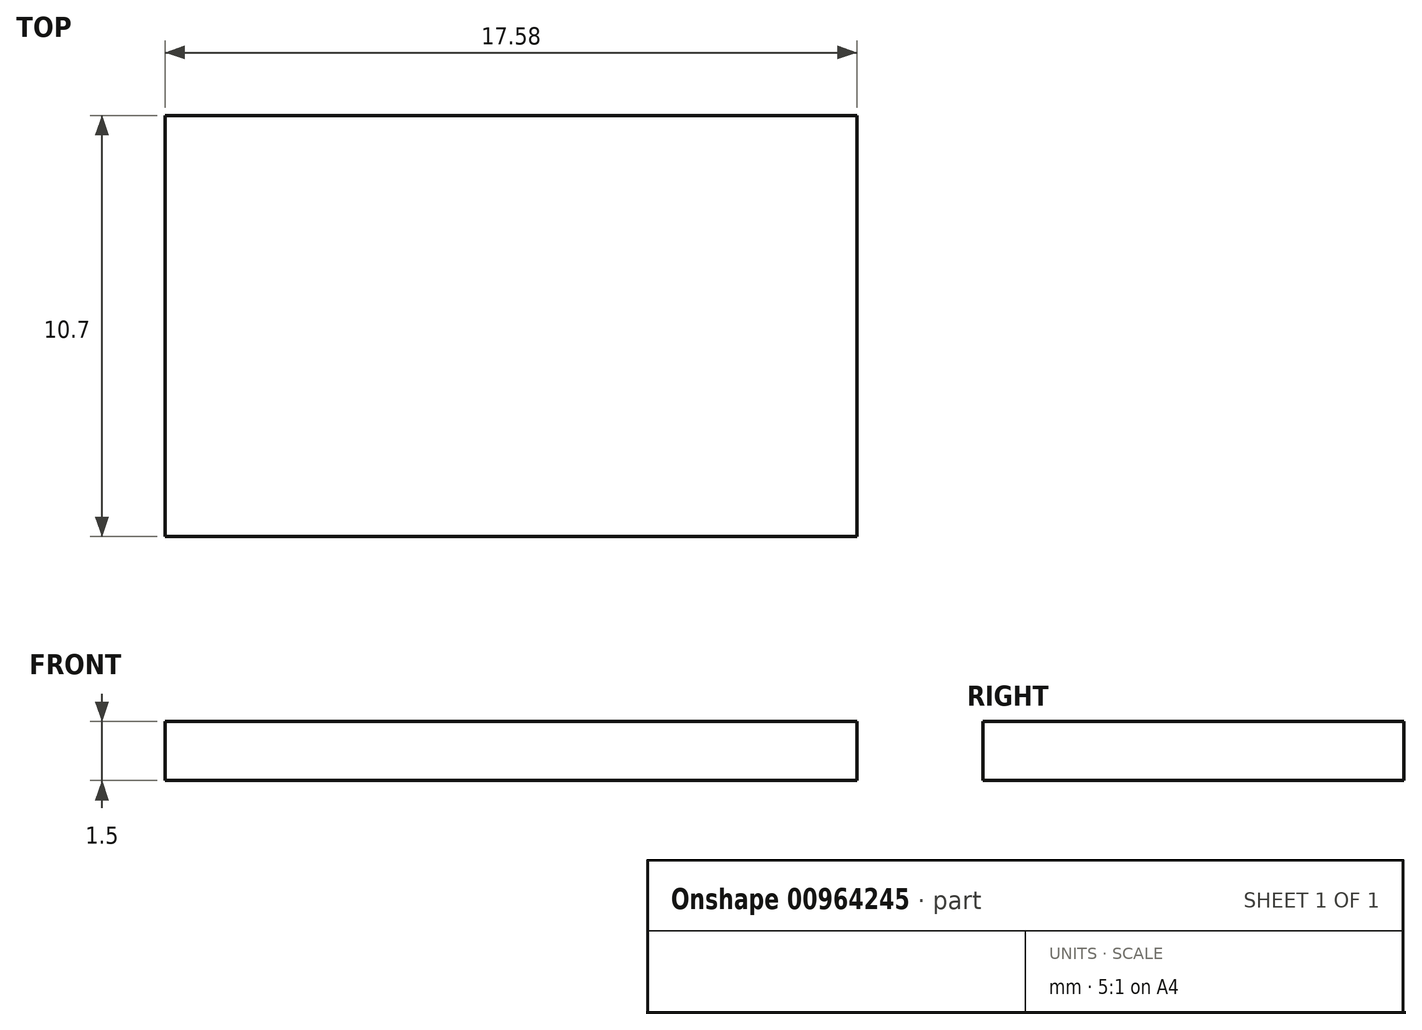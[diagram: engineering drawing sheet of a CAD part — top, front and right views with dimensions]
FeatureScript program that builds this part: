
annotation { "Feature Type Name" : "Feature", "Feature Type Description" : "" }
export const myFeature = defineFeature(function(context is Context, id is Id, definition is map)
    precondition{}
    {
        {
            var Q0;
            Q0=qCreatedBy(makeId("Top.planeOp"),FACE);
            var sketch = newSketch(context, id + "F0", { "sketchPlane" : qUnion([Q0])});
            skLineSegment(sketch, "E0.bottom", {"start": v(-8.79, 5.35) * mm, "end": v(8.8, 5.35) * mm});
            skLineSegment(sketch, "E0.top", {"start": v(-8.8, -5.35) * mm, "end": v(8.79, -5.35) * mm});
            skLineSegment(sketch, "E0.left", {"start": v(-8.79, 5.35) * mm, "end": v(-8.8, -5.35) * mm});
            skLineSegment(sketch, "E0.right", {"start": v(8.8, 5.35) * mm, "end": v(8.79, -5.35) * mm});
            skLineSegment(sketch, "E1", {"start": v(-8.79, 5.35) * mm, "end": v(8.79, -5.35) * mm, "construction": true});
            skLineSegment(sketch, "E2", {"start": v(8.8, 5.35) * mm, "end": v(-8.8, -5.35) * mm, "construction": true});
            skPoint(sketch, "E3", {"position": v(0, 0) * mm});
            skSolve(sketch);
        }
        {
            var Q0;
            Q0 = qSketchRegion(id + "F0", true);
            extrude(context, id + "F1", {"entities" : qUnion([Q0]), "depth" : 1.5 * mm, "offsetDistance" : 25 * mm});
        }
    });
